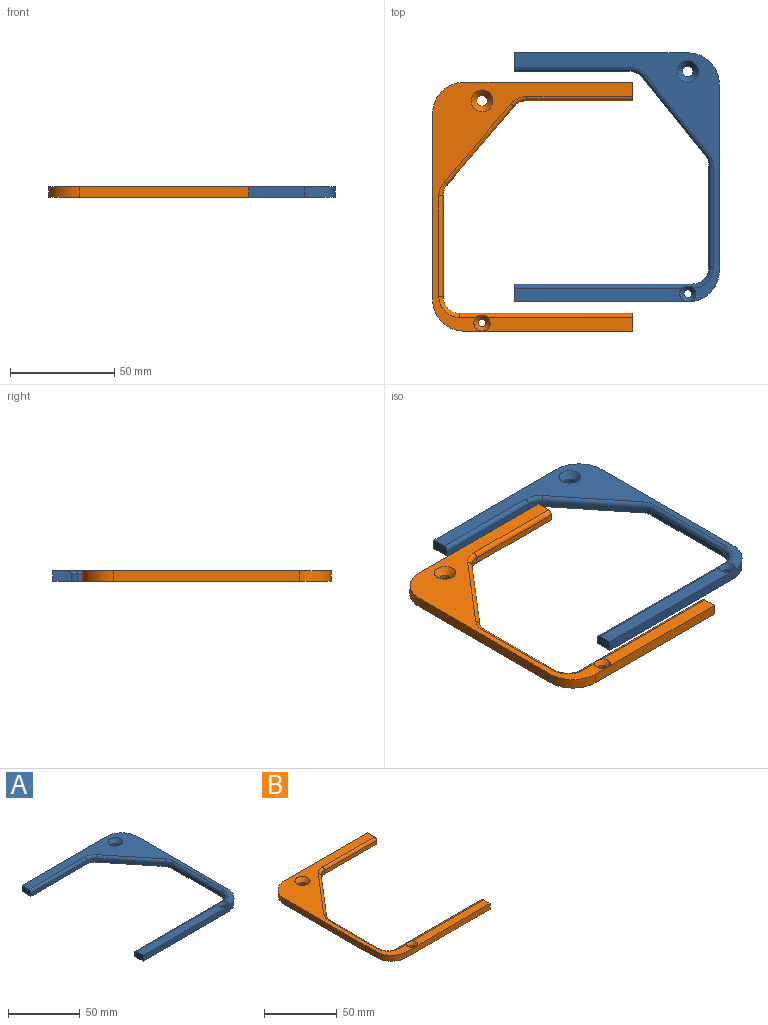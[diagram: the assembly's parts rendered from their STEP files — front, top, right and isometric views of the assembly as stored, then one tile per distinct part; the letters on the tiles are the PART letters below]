
ASSEMBLY  parts=2 mates=1
PART A: 28 faces, bbox 98.3x119.3x5 mm
  f0: plane 82.77x6.5mm, normal (0,0,1), area 518.9mm2, adj f2,f10,f15,f27
  f1: plane 119.23x98.27mm, normal (0,0,1), area 1689.2mm2, adj f3,f4,f11,f13,f15,f19,f20,f21
  f2: plane 83.29x5.03mm, normal (0,-1,0), area 416.3mm2, adj f0,f9,f10,f15,f20
  f3: plane 83.27x5mm, normal (0,1,0), area 416.3mm2, adj f1,f4,f9,f19
  f4: plane 8.86x5mm, normal (-1,0,0), area 43.4mm2, adj f1,f3,f5,f9,f21
  f5: plane 55.12x3mm, normal (0,-1,0), area 165.3mm2, adj f4,f9,f16,f21
  f6: plane 37.47x30.15mm, normal (-0.78,-0.63,0), area 144.3mm2, adj f9,f16,f17,f23
  f7: plane 48.41x3mm, normal (-1,0,0), area 145.2mm2, adj f9,f17,f18,f25
  f8: plane 85.27x3mm, normal (0,1,0), area 255.8mm2, adj f9,f10,f18,f27
  f9: plane 119.23x98.27mm, normal (0,0,-1), area 2834.8mm2, adj f2,f3,f4,f5,f6,f7,f8,f10
  f10: plane 8.5x5mm, normal (-1,0,0), area 41.6mm2, adj f0,f2,f8,f9,f27
  f11: plane 89.23x5mm, normal (1,0,0), area 446.2mm2, adj f1,f9,f19,f20
  f12: cylinder r=2.55mm len=5.11mm, axis (0,0,1), area 31mm2, adj f9,f13
  f13: cone r=2.55mm half-angle=41deg, axis (0,0,1), area 99.3mm2, adj f1,f12
  f14: cylinder r=1.9mm len=3.8mm, axis (0,0,1), area 32.2mm2, adj f9,f15
  f15: cone r=1.9mm half-angle=41deg, axis (0,0,1), area 54.2mm2, adj f0,f1,f2,f14,f20,f26,f27
  f16: cylinder r=8mm len=6.23mm, axis (0,0,1), area 21.4mm2, adj f5,f6,f9,f22
  f17: cylinder r=8mm len=5.02mm, axis (0,0,1), area 16.3mm2, adj f6,f7,f9,f24
  f18: cylinder r=8mm len=8mm, axis (0,0,1), area 37.7mm2, adj f7,f8,f9,f26
  f19: cylinder r=15mm len=15mm, axis (0,0,-1), area 117.8mm2, adj f1,f3,f9,f11
  f20: cylinder r=15mm len=15mm, axis (0,0,1), area 117.8mm2, adj f1,f2,f9,f11,f15
  f21: cylinder r=2mm len=55.12mm, axis (-1,0,0), area 173.1mm2, adj f1,f4,f5,f22
  f22: torus R=10mm, axis (0,0,1), area 24.5mm2, adj f1,f16,f21,f23
  f23: cylinder r=2mm len=38.72mm, axis (-0.63,0.78,0), area 151.1mm2, adj f1,f6,f22,f24
  f24: torus R=10mm, axis (0,0,1), area 18.6mm2, adj f1,f17,f23,f25
  f25: cylinder r=2mm len=48.41mm, axis (0,1,0), area 152.1mm2, adj f1,f7,f24,f26
  f26: torus R=10mm, axis (0,0,1), area 42.9mm2, adj f1,f15,f18,f25,f27
  f27: cylinder r=2mm len=85.27mm, axis (1,0,0), area 263.7mm2, adj f0,f8,f10,f15,f26
PART B: 28 faces, bbox 95.8x119.3x5.1 mm
  f0: plane 71.72x6.5mm, normal (0,0,1), area 447.1mm2, adj f2,f8,f14,f27
  f1: plane 119.23x95.78mm, normal (0,0,1), area 1775.6mm2, adj f2,f5,f6,f7,f13,f14,f19,f20
  f2: plane 80.83x5.06mm, normal (0,-1,0), area 403.9mm2, adj f0,f1,f8,f11,f14,f20
  f3: plane 37.6x32.18mm, normal (0.76,-0.65,0), area 148.5mm2, adj f11,f16,f18,f23
  f4: plane 50.6x3mm, normal (0,-1,0), area 151.8mm2, adj f5,f11,f16,f21
  f5: plane 8.86x5mm, normal (1,0,0), area 43.4mm2, adj f1,f4,f6,f11,f21
  f6: plane 80.78x5mm, normal (0,1,0), area 403.9mm2, adj f1,f5,f11,f19
  f7: plane 89.23x5mm, normal (-1,0,0), area 446.2mm2, adj f1,f11,f19,f20
  f8: plane 8.5x5mm, normal (1,0,0), area 41.6mm2, adj f0,f2,f9,f11,f27
  f9: plane 82.78x3mm, normal (0,1,0), area 248.3mm2, adj f8,f11,f17,f27
  f10: plane 48.28x3mm, normal (1,0,0), area 144.8mm2, adj f11,f17,f18,f25
  f11: plane 119.23x95.78mm, normal (0,0,-1), area 2838mm2, adj f2,f3,f4,f5,f6,f7,f8,f9
  f12: cylinder r=2.55mm len=5.11mm, axis (0,0,1), area 31mm2, adj f11,f13
  f13: cone r=2.55mm half-angle=41deg, axis (0,0,1), area 99.3mm2, adj f1,f12
  f14: cone r=1.9mm half-angle=41deg, axis (0,0,1), area 54.2mm2, adj f0,f1,f2,f15,f27
  f15: cylinder r=1.9mm len=3.8mm, axis (0,0,1), area 32.2mm2, adj f11,f14
  f16: cylinder r=8mm len=6.08mm, axis (0,0,1), area 20.7mm2, adj f3,f4,f11,f22
  f17: cylinder r=8mm len=8mm, axis (0,0,1), area 37.7mm2, adj f9,f10,f11,f26
  f18: cylinder r=8mm len=5.2mm, axis (0,0,1), area 17mm2, adj f3,f10,f11,f24
  f19: cylinder r=15mm len=15mm, axis (0,0,-1), area 117.8mm2, adj f1,f6,f7,f11
  f20: cylinder r=15mm len=15mm, axis (0,0,1), area 117.8mm2, adj f1,f2,f7,f11
  f21: cylinder r=2mm len=50.6mm, axis (-1,0,0), area 159mm2, adj f1,f4,f5,f22
  f22: torus R=10mm, axis (0,0,1), area 23.7mm2, adj f1,f16,f21,f23
  f23: cylinder r=2mm len=38.9mm, axis (-0.65,-0.76,0), area 155.5mm2, adj f1,f3,f22,f24
  f24: torus R=10mm, axis (0,0,1), area 19.4mm2, adj f1,f18,f23,f25
  f25: cylinder r=2mm len=48.28mm, axis (0,-1,0), area 151.7mm2, adj f1,f10,f24,f26
  f26: torus R=10mm, axis (0,0,1), area 43.1mm2, adj f1,f17,f25,f27
  f27: cylinder r=2mm len=82.78mm, axis (1,0,0), area 255.7mm2, adj f0,f1,f8,f9,f14,f26
PLACE A t=(158.35,14.06,110.79)mm
PLACE B t=(0,0,110.79)mm
MATE planar A.f19 <-> B.f19  axis (0,0,-1) through (58.58,58.68,110.79)mm
